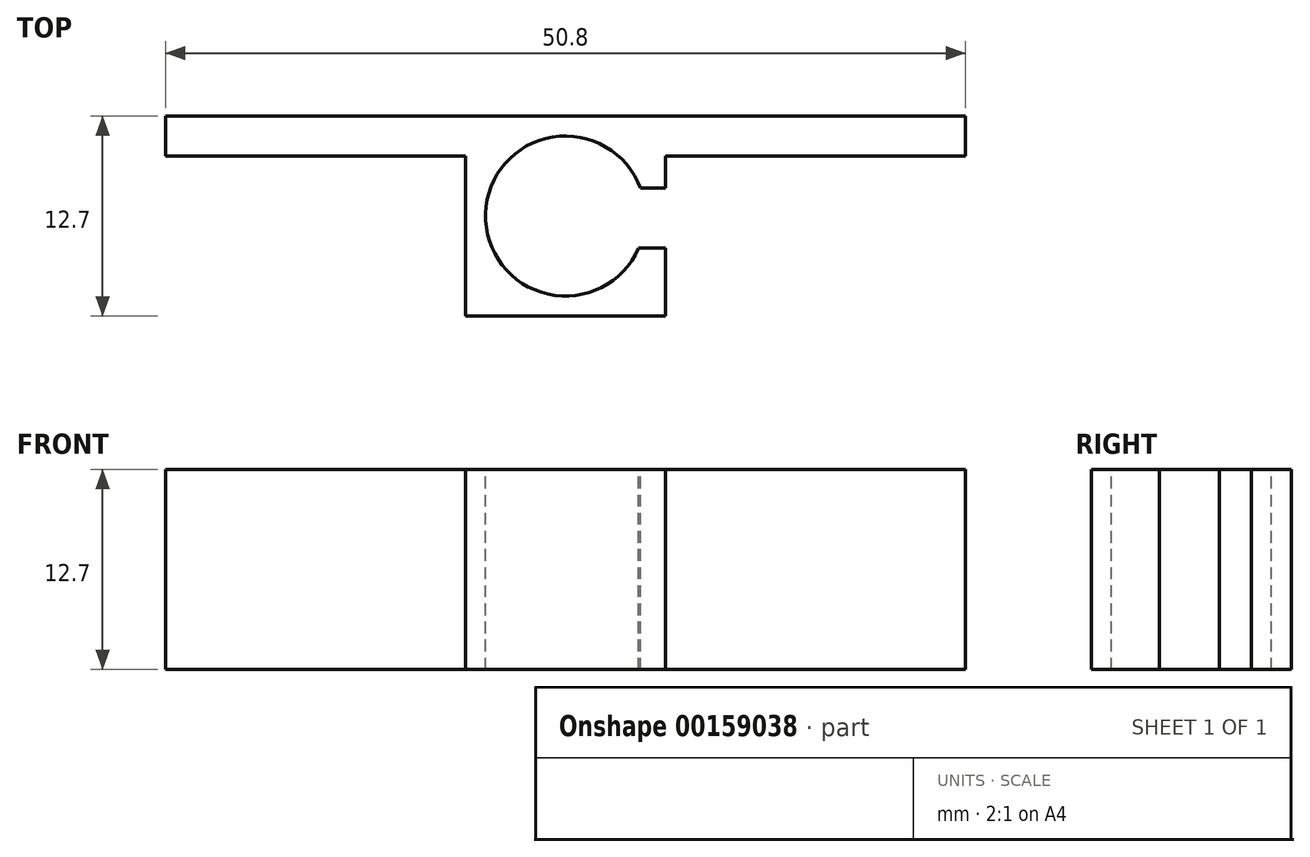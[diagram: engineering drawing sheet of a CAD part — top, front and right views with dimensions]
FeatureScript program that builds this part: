
annotation { "Feature Type Name" : "Feature", "Feature Type Description" : "" }
export const myFeature = defineFeature(function(context is Context, id is Id, definition is map)
    precondition{}
    {
        {
            var Q0;
            Q0=qCreatedBy(makeId("Front.planeOp"),FACE);
            var sketch = newSketch(context, id + "F0", { "sketchPlane" : qUnion([Q0])});
            skLineSegment(sketch, "E0.bottom", {"start": v(-38.62, 17.62) * mm, "end": v(-25.92, 17.62) * mm});
            skLineSegment(sketch, "E0.top", {"start": v(-38.62, 4.92) * mm, "end": v(-25.92, 4.92) * mm});
            skLineSegment(sketch, "E0.left", {"start": v(-38.62, 17.62) * mm, "end": v(-38.62, 4.92) * mm});
            skLineSegment(sketch, "E0.right", {"start": v(-25.92, 17.62) * mm, "end": v(-25.92, 4.92) * mm});
            skSolve(sketch);
        }
        {
            var Q0;
            Q0=makeQuery(id+"F0.imprint","IMPRINT",FACE,{"disambiguationData":[TD([[makeQuery(id+"F0.imprint","IMPRINT",EDGE,{"derivedFrom":sQuery(id+"F0.wireOp",EDGE,"E0.bottom")}),-1.0]])]});
            extrude(context, id + "F1", {"entities" : qUnion([Q0]), "oppositeDirection" : true, "depth" : 12.7 * mm});
        }
        {
            var Q0;
            Q0=makeQuery(id+"F1.opExtrude","SWEPT_FACE",FACE,{"disambiguationData":[OSD([sQuery(id+"F0.wireOp",EDGE,"E0.bottom")])]});
            var sketch = newSketch(context, id + "F2", { "sketchPlane" : qUnion([Q0])});
            skArc(sketch, "E1", {"start": v(-27.51, 8.12) * mm, "mid": v(-37.35, 6.5) * mm, "end": v(-27.62, 4.3) * mm});
            skPoint(sketch, "E1.centerSnap0", {"position": v(-38.62, 6.35) * mm});
            skPoint(sketch, "E1.centerSnap1", {"position": v(-32.27, 12.7) * mm});
            skLineSegment(sketch, "E2", {"start": v(-27.51, 8.12) * mm, "end": v(-25.92, 8.12) * mm});
            skLineSegment(sketch, "E3", {"start": v(-27.62, 4.3) * mm, "end": v(-25.92, 4.3) * mm});
            skLineSegment(sketch, "E4", {"start": v(-25.92, 22.1) * mm, "end": v(-17.46, 22.1) * mm});
            skLineSegment(sketch, "E5", {"start": v(-17.46, 12.7) * mm, "end": v(-17.46, 22.1) * mm});
            skLineSegment(sketch, "E6", {"start": v(-17.46, 12.7) * mm, "end": v(-25.92, 12.7) * mm});
            skLineSegment(sketch, "E7", {"start": v(-38.62, 22.1) * mm, "end": v(-47.1, 22.1) * mm});
            skLineSegment(sketch, "E8", {"start": v(-47.1, 12.7) * mm, "end": v(-47.1, 22.1) * mm});
            skLineSegment(sketch, "E9", {"start": v(-47.1, 12.7) * mm, "end": v(-38.62, 12.7) * mm});
            skLineSegment(sketch, "E10", {"start": v(-25.92, 12.7) * mm, "end": v(-25.92, 22.1) * mm});
            skLineSegment(sketch, "E11", {"start": v(-38.62, 12.7) * mm, "end": v(-38.62, 22.1) * mm});
            skPoint(sketch, "E12", {"position": v(-25.92, 6.35) * mm});
            skSolve(sketch);
        }
        {
            var Q0;
            Q0=makeQuery(id+"F2.imprint","IMPRINT",FACE,{"disambiguationData":[TD([[makeQuery(id+"F2.imprint","IMPRINT",EDGE,{"derivedFrom":sQuery(id+"F2.wireOp",EDGE,"E1")}),1.0]])]});
            extrude(context, id + "F3", {"entities" : qUnion([Q0]), "operationType" : NewBodyOperationType.REMOVE, "oppositeDirection" : true, "depth" : 38.1 * mm});
        }
        {
            var Q0;
            Q0=makeQuery(id+"F1.opExtrude","CAP_FACE",FACE,{"disambiguationData":[OSD([sQuery(id+"F0.wireOp",EDGE,"E0.bottom"),sQuery(id+"F0.wireOp",EDGE,"E0.top"),sQuery(id+"F0.wireOp",EDGE,"E0.left"),sQuery(id+"F0.wireOp",EDGE,"E0.right")])],"isStart":false});
            var sketch = newSketch(context, id + "F4", { "sketchPlane" : qUnion([Q0])});
            skLineSegment(sketch, "E13", {"start": v(25.92, 4.92) * mm, "end": v(6.87, 4.92) * mm});
            skLineSegment(sketch, "E14", {"start": v(6.87, 4.92) * mm, "end": v(6.87, 17.62) * mm});
            skLineSegment(sketch, "E15", {"start": v(6.87, 17.62) * mm, "end": v(25.92, 17.62) * mm});
            skLineSegment(sketch, "E16", {"start": v(38.62, 17.62) * mm, "end": v(38.62, 4.92) * mm});
            skLineSegment(sketch, "E17", {"start": v(38.62, 4.92) * mm, "end": v(57.67, 4.92) * mm});
            skLineSegment(sketch, "E18", {"start": v(57.67, 4.92) * mm, "end": v(57.67, 17.62) * mm});
            skLineSegment(sketch, "E19", {"start": v(57.67, 17.62) * mm, "end": v(38.62, 17.62) * mm});
            skSolve(sketch);
        }
        {
            var Q0;
            Q0=makeQuery(id+"F4.imprint","IMPRINT",FACE,{"disambiguationData":[TD([[makeQuery(id+"F4.imprint","IMPRINT",EDGE,{"derivedFrom":sQuery(id+"F4.wireOp",EDGE,"E16")}),1.0]])]});
            var Q1;
            Q1=makeQuery(id+"F4.imprint","IMPRINT",FACE,{"disambiguationData":[TD([[makeQuery(id+"F4.imprint","IMPRINT",EDGE,{"derivedFrom":sQuery(id+"F4.wireOp",EDGE,"E13")}),-1.0]])]});
            extrude(context, id + "F5", {"entities" : qUnion([Q0, Q1]), "operationType" : NewBodyOperationType.ADD, "oppositeDirection" : true, "depth" : 2.54 * mm});
        }
    });
